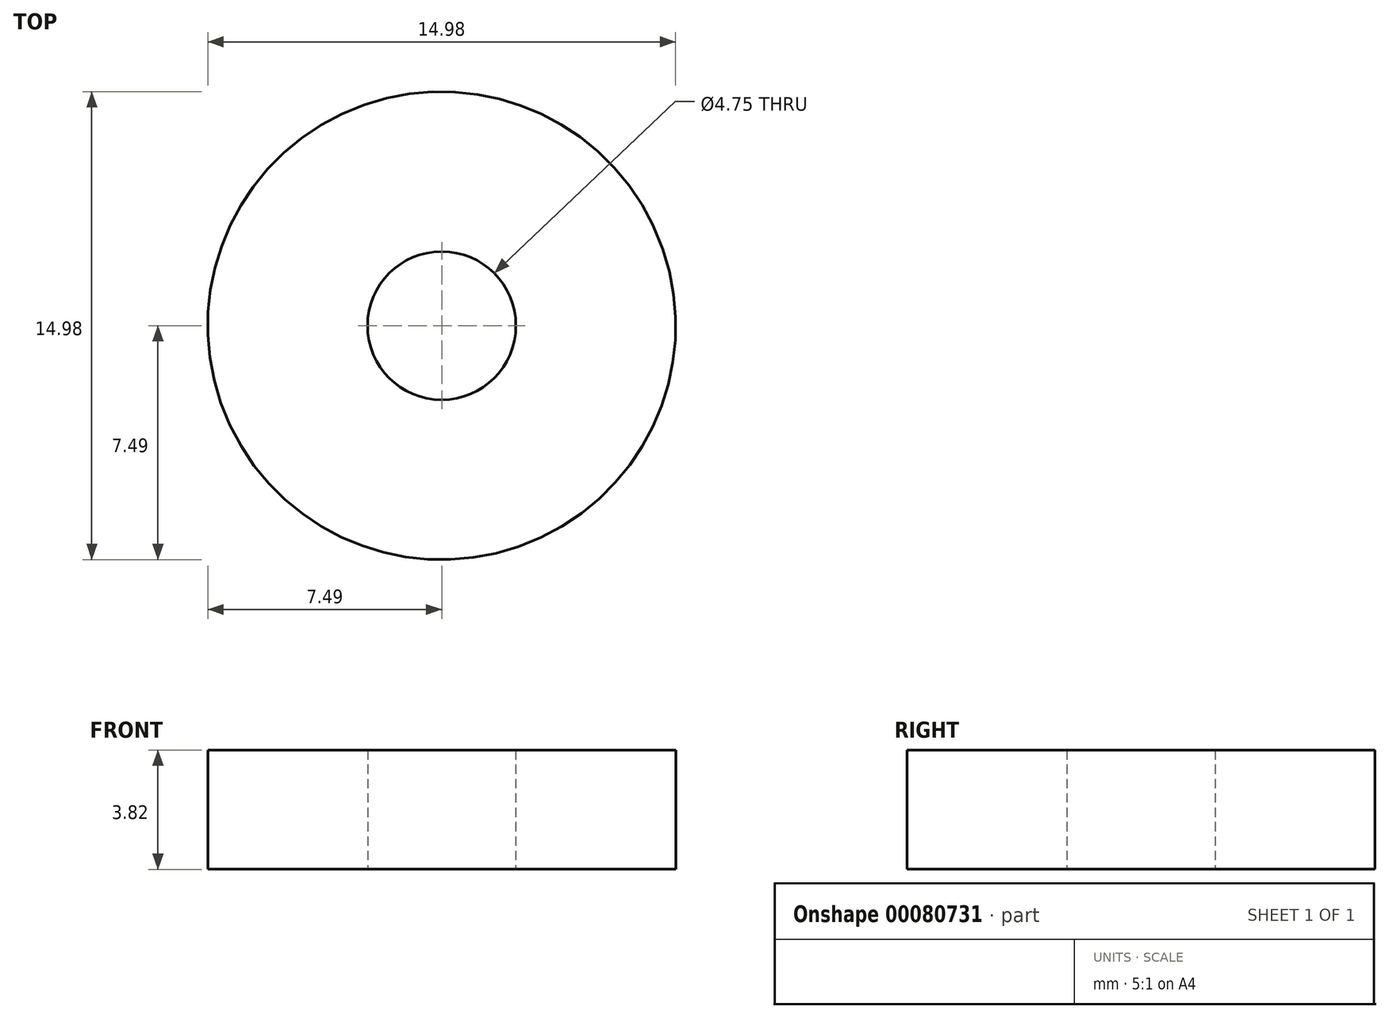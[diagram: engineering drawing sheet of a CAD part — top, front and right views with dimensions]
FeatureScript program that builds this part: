
annotation { "Feature Type Name" : "Feature", "Feature Type Description" : "" }
export const myFeature = defineFeature(function(context is Context, id is Id, definition is map)
    precondition{}
    {
        {
            var Q0;
            Q0=qCreatedBy(makeId("Top.planeOp"),FACE);
            var sketch = newSketch(context, id + "F0", { "sketchPlane" : qUnion([Q0])});
            skCircle(sketch, "E0", {"center": v(0, 0) * mm, "radius": 50.8 * mm});
            skCircle(sketch, "E1", {"center": v(0, 0) * mm, "radius": 2.37 * mm});
            skCircle(sketch, "E2", {"center": v(0, 0) * mm, "radius": 7.5 * mm});
            skFitSpline(sketch, "E3", {"points": [v(-7.33, 1.58) * mm, v(-11.96, 49.37) * mm], "startDerivative": vector(-34.7, 51.98) * mm, "endDerivative": vector(54.42, 32.42) * mm});
            skFitSpline(sketch, "E4", {"points": [v(6.8, 3.16) * mm, v(24.25, 44.64) * mm], "startDerivative": vector(-20.38, 43.44) * mm, "endDerivative": vector(72.54, 15) * mm});
            skFitSpline(sketch, "E5", {"points": [v(8.6, 50.07) * mm, v(-11.7, 61.01) * mm, v(-5.7, 50.48) * mm], "startDerivative": vector(-14.05, 50.07) * mm, "endDerivative": vector(-40.72, -66.06) * mm});
            skCircle(sketch, "E6", {"center": v(0, 0) * mm, "radius": 44.45 * mm});
            skFitSpline(sketch, "E7", {"points": [v(-3.48, 6.63) * mm, v(-5.7, 50.48) * mm], "startDerivative": vector(-30.89, 42.81) * mm, "endDerivative": vector(51.45, 37.06) * mm});
            skFitSpline(sketch, "E8", {"points": [v(1.93, 7.24) * mm, v(18.5, 47.31) * mm], "startDerivative": vector(-19.74, 24.24) * mm, "endDerivative": vector(74.82, 23.94) * mm});
            skCircle(sketch, "E9", {"center": v(0, 0) * mm, "radius": 29.15 * mm});
            skCircle(sketch, "E10", {"center": v(0, 0) * mm, "radius": 22.8 * mm});
            skLineSegment(sketch, "E11", {"start": v(-44.45, 0) * mm, "end": v(-29.15, 0) * mm, "construction": true});
            skLineSegment(sketch, "E12", {"start": v(-22.8, 0) * mm, "end": v(-7.5, 0) * mm, "construction": true});
            skLineSegment(sketch, "E13", {"start": v(22.8, 0) * mm, "end": v(29.15, 0) * mm, "construction": true});
            skLineSegment(sketch, "E14", {"start": v(44.45, 0) * mm, "end": v(50.8, 0) * mm, "construction": true});
            skCircle(sketch, "E15", {"center": v(0, 0) * mm, "radius": 36.8 * mm});
            skLineSegment(sketch, "E16", {"start": v(29.15, 0) * mm, "end": v(36.8, 0) * mm, "construction": true});
            skLineSegment(sketch, "E17", {"start": v(36.8, 0) * mm, "end": v(44.45, 0) * mm, "construction": true});
            skFitSpline(sketch, "E18", {"points": [v(0, 32.1) * mm, v(-11.28, 35.03) * mm], "startDerivative": vector(-3.5, 5.56) * mm, "endDerivative": vector(-20.7, -1.7) * mm});
            skCircle(sketch, "E19", {"center": v(0, 0) * mm, "radius": 15.14 * mm});
            skLineSegment(sketch, "E20", {"start": v(7.5, 0) * mm, "end": v(15.14, 0) * mm, "construction": true});
            skLineSegment(sketch, "E21", {"start": v(15.14, 0) * mm, "end": v(22.8, 0) * mm, "construction": true});
            skFitSpline(sketch, "E22", {"points": [v(-1.08, 13.13) * mm, v(-6.62, 13.62) * mm], "startDerivative": vector(-5.42, 2.86) * mm, "endDerivative": vector(-10.03, -1.88) * mm});
            skSolve(sketch);
        }
        {
            var Q0;
            Q0=makeQuery(id+"F0.imprint","IMPRINT",FACE,{"disambiguationData":[TD([[makeQuery(id+"F0.imprint","IMPRINT",EDGE,{"derivedFrom":sQuery(id+"F0.wireOp",EDGE,"E1")}),-1.0]])]});
            extrude(context, id + "F1", {"entities" : qUnion([Q0]), "endBound" : BoundingType.SYMMETRIC, "depth" : 3.8 * mm});
        }
    });
